# Revit family: Desks-Preconfigured-Teknion-B_YRG_Single_Pedestal_Half_Glass_Modesty-R2015
name_source: partatom
category: Furniture
revit_build: Autodesk Revit Architecture 2015 (Build: 20140323_1530(x64)
units: mm (PartAtom-declared; Revit-internal decimal feet)

## types (1)
- 1-3/16" Thick WS
    Assembly Code = E2020200
    Description = Rectangular Executive Desk with Single Pedestal – Half Glass Modesty, 1-3/16" Thick WS
    Manufacturer = Teknion
    Manufacturer Fax = 416.661.4586
    Model = BMYRG___
    Part Number = B_YRG
    Product Documentation Link = http://www.teknion.com
    Product Line = Expansion Casegoods
    Product Page URL = http://www.teknion.com
    Series = Expansion Casegoods
    Sustainability Data = http://www.teknion.com
    URL = http://www.teknion.com
    Unit Weight URL = http://www.teknion.com
    Warranty = http://www.teknion.com
    Worksurface Thickness = 1.188 "

## geometry (parser evidence)
native form markers: Blend x145, Sweep x2
no freeform markers — native parametric forms only
